# Revit family: QF_BPRO_WBS 400x320x150_566228
name_source: partatom
category: Sonderausstattung
revit_build: Autodesk Revit 2018 (Build: 20190510_1515(x64)
units: mm (PartAtom-declared; Revit-internal decimal feet)

## family parameters
Arbeitsebenenbasiert = Nein
Beim Laden mit Abzugskörper schneiden = Nein
Bemaßung runder Anschluss = Durchmesser verwenden
Gemeinsam genutzt = Nein
Immer vertikal = Ja
Raumberechnungspunkt = Ja
Teiletyp = Normal

## types (1)
- WBS 4 x 3,2 x 1,5
    Abstand TWW zu TWK = 100 mm  [stored 0.328084 ft]
    Artikel Nummer = 566228
    Aufkantung = Ja
    Beschreibung = Handwaschbecken mit 3-seitiger Beckenverkleidung, mit selektiv gesteuerter Armatur
    Beschreibung durch Hersteller analog Leistungsverzeichniskurztext = Abmessungen:

Länge:   	400 mm
Breite:  	320 mm
Höhe:     150/180 mm

Beckengröße: 
Länge:   	340 mm
Breite:  	240 mm
Tiefe:   	150 mm


Ausführung:

Die Abdeckung dreiseitig abgekantet und an der Rückseite aufgekantet. Darin fugenlos eingeschweißt 1 tiefgezogenes Waschbecken. Auslaufprägung 1 1/2", mit Überlaufsicherung, ohne Ventil. 
Mit berührungsloser Armatur 1/2" (Modell GIATRONIC). Die Temperatur ist mittels hinten angeordnetem Hebel individuell von kalt bis warm einstellbar. Sobald die Hände unter die Armatur gehalten werden, fließt automatisch das Wasser
in der vorgewählten Temperatur, bei Wegziehen stoppt automatisch der Wasserfluss. Der Trafo wird im Unterbereich mit Netzanschluss von 230 V 50 HZ und entsprechendem Anschlusskabel eingebaut. Angeschweißt 2 Konsolen aus Chromnickelstahl. Mit dreiseitiger Beckenverkleidung aus CNS, 150 mm hoch. 


Technische Daten:

Werkstoff:         		CNS 18/10
Werkstoff-Nr.:		1.4301


Fabrikat:

Hersteller:        		B.PRO
Typ:               		WBS 4 x 3,2 x 1,5

Best.-Nr.:         		566 228
    Beschreibung durch Hersteller analog Leistungsverzeichnislangtext = Abmessungen:

Länge:   	400 mm
Breite:  	320 mm
Höhe:     150/180 mm

Beckengröße: 
Länge:   	340 mm
Breite:  	240 mm
Tiefe:   	150 mm


Ausführung:

Die Abdeckung dreiseitig abgekantet und an der Rückseite aufgekantet. Darin fugenlos eingeschweißt 1 tiefgezogenes Waschbecken. Auslaufprägung 1 1/2", mit Überlaufsicherung, ohne Ventil. 
Mit berührungsloser Armatur 1/2" (Modell GIATRONIC). Die Temperatur ist mittels hinten angeordnetem Hebel individuell von kalt bis warm einstellbar. Sobald die Hände unter die Armatur gehalten werden, fließt automatisch das Wasser
in der vorgewählten Temperatur, bei Wegziehen stoppt automatisch der Wasserfluss. Der Trafo wird im Unterbereich mit Netzanschluss von 230 V 50 HZ und entsprechendem Anschlusskabel eingebaut. Angeschweißt 2 Konsolen aus Chromnickelstahl. Mit dreiseitiger Beckenverkleidung aus CNS, 150 mm hoch. 


Technische Daten:

Werkstoff:         		CNS 18/10
Werkstoff-Nr.:		1.4301


Fabrikat:

Hersteller:        		B.PRO
Typ:               		WBS 4 x 3,2 x 1,5

Best.-Nr.:         		566 228
    CE Kennzeichnung = Ja
    Direkte Ablaufanschlussgröße = 40 mm
    Direkter Abwasserstrom = 0.0 L/s
    Frequenz = 50 Hz
    Gerätegewicht Netto = 0.00 kg
    Großküchengerätezuordnung = Ja
    Hersteller = B.PRO GmbH
    Höhe = 200 mm
    Internetadresse Gerätehersteller = https://www.bpro-solutions.com
    Internetadresse für Ersatzteilliste = https://www.bpro-solutions.com
    Kaltwasser Durchflussmenge = 0.0 L/s
    Kaltwasseranschlussgröße = 15 mm
    Kaltwasserdruck Maximum = 0.0 Pa
    Kaltwasserdruck Minimum = 0.0 Pa
    Kosten = 839 $
    Länge Gerätebreite = 400 mm  [stored 1.31234 ft]
    Material = <Nach Kategorie>
    Modell = WBS 4 x 3,2 x 1,5
    Siphon am Gerät = Nein
    Spannung = 230 V
    Tiefe = 320 mm
    Typenkommentare = Handwaschbecken mit 3-seitiger Beckenverkleidung, mit selektiv gesteuerter Armatur
    URL = https://www.bpro-solutions.com
    Warmwasser Durchflussmenge = 0.0 L/s
    Warmwasseranschlussgröße = 15 mm
    Warmwasserdruck Maximum = 0.0 Pa
    Warmwasserdruck Minimum = 0.0 Pa
    Zubehör = Ja

note: [stored X ft] marks values corroborated as IEEE doubles in the binary element streams (Revit-internal decimal feet)
